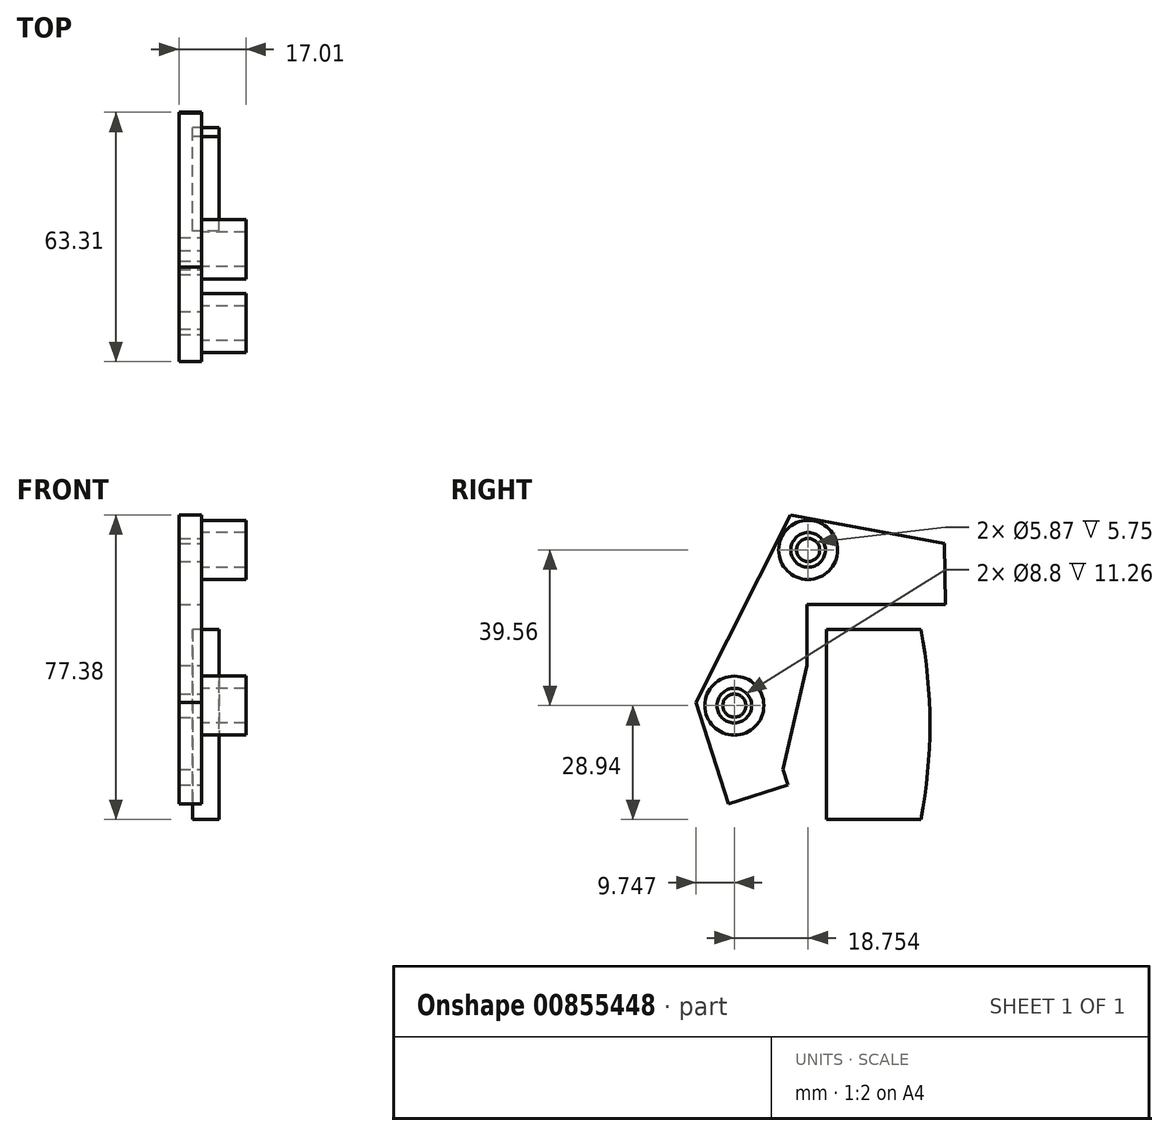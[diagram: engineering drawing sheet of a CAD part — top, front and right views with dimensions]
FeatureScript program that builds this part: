
annotation { "Feature Type Name" : "Feature", "Feature Type Description" : "" }
export const myFeature = defineFeature(function(context is Context, id is Id, definition is map)
    precondition{}
    {
        {
            var Q0;
            Q0=qCreatedBy(makeId("Right.planeOp"),FACE);
            var sketch = newSketch(context, id + "F0", { "sketchPlane" : qUnion([Q0])});
            skLineSegment(sketch, "E0.bottom", {"start": v(101.64, 24.15) * mm, "end": v(125.64, 24.15) * mm});
            skLineSegment(sketch, "E0.top", {"start": v(101.64, -24.15) * mm, "end": v(125.64, -24.15) * mm});
            skLineSegment(sketch, "E0.left", {"start": v(101.64, 24.15) * mm, "end": v(101.64, -24.15) * mm});
            skLineSegment(sketch, "E0.right", {"start": v(125.64, 24.15) * mm, "end": v(125.64, -24.15) * mm});
            skCircle(sketch, "E1", {"center": v(0, 0) * mm, "radius": 127.94 * mm});
            skPoint(sketch, "E1.third.point", {"position": v(127.94, 0) * mm});
            skPoint(sketch, "E1.third.point.positionSnap0", {"position": v(125.64, 0) * mm});
            skSolve(sketch);
        }
        {
            var Q0;
            Q0=makeQuery(id+"F0.imprint","IMPRINT",FACE,{"disambiguationData":[TD([[makeQuery(id+"F0.imprint","IMPRINT",EDGE,{"derivedFrom":sQuery(id+"F0.wireOp",EDGE,"E0.bottom")}),-1.0]])]});
            var Q1;
            {var subQ0=sQuery(id+"F0.wireOp",EDGE,"E0.right");Q1=makeQuery(id+"F0.imprint","IMPRINT",FACE,{"disambiguationData":[TD([[makeQuery(id+"F0.imprint","IMPRINT",EDGE,{"derivedFrom":subQ0}),1.0]])]});}
            extrude(context, id + "F1", {"entities" : qUnion([Q0, Q1]), "depth" : 6.8 * mm, "offsetDistance" : 25 * mm});
        }
        {
            var Q0;
            Q0=makeQuery(id+"F1.opExtrude","CAP_FACE",FACE,{"disambiguationData":[OSD([sQuery(id+"F0.wireOp",EDGE,"E0.bottom"),sQuery(id+"F0.wireOp",EDGE,"E0.top"),sQuery(id+"F0.wireOp",EDGE,"E0.left"),sQuery(id+"F0.wireOp",EDGE,"E1")])],"isStart":true});
            cPlane(context, id + "F2", {"entities" : qUnion([Q0]), "cplaneType" : CPlaneType.OFFSET, "offset" : 2.3 * mm, "oppositeDirection" : true, "width" : 150 * mm, "height" : 150 * mm});
        }
        {
            var Q0;
            Q0=qCreatedBy(id+"F2.planeOp",FACE);
            var sketch = newSketch(context, id + "F3", { "sketchPlane" : qUnion([Q0])});
            skLineSegment(sketch, "E2.0.0", {"start": v(-101.64, 24.15) * mm, "end": v(-101.64, -24.15) * mm});
            skLineSegment(sketch, "E2.0.1", {"start": v(-101.64, -24.15) * mm, "end": v(-125.64, -24.15) * mm});
            skArc(sketch, "E2.0.2", {"start": v(-125.64, -24.15) * mm, "mid": v(-127.94, 0) * mm, "end": v(-125.64, 24.15) * mm});
            skLineSegment(sketch, "E2.0.3", {"start": v(-125.64, 24.15) * mm, "end": v(-101.64, 24.15) * mm});
            skPoint(sketch, "E3", {"position": v(-78.26, 4.8) * mm});
            skPoint(sketch, "E4", {"position": v(-97.01, 44.35) * mm});
            skLineSegment(sketch, "E5", {"start": v(-131.61, 45.95) * mm, "end": v(-92.51, 53.23) * mm});
            skLineSegment(sketch, "E6", {"start": v(-92.51, 53.23) * mm, "end": v(-68.51, 5.54) * mm});
            skLineSegment(sketch, "E7", {"start": v(-68.51, 5.54) * mm, "end": v(-76.8, -20.15) * mm});
            skLineSegment(sketch, "E8", {"start": v(-76.8, -20.15) * mm, "end": v(-91.83, -15.3) * mm});
            skLineSegment(sketch, "E9", {"start": v(-91.83, -15.3) * mm, "end": v(-90.57, -11.4) * mm});
            skLineSegment(sketch, "E10", {"start": v(-90.57, -11.4) * mm, "end": v(-96.68, 15.04) * mm});
            skLineSegment(sketch, "E11", {"start": v(-96.68, 15.04) * mm, "end": v(-96.68, 30.5) * mm});
            skLineSegment(sketch, "E12", {"start": v(-96.68, 30.5) * mm, "end": v(-131.82, 30.5) * mm});
            skLineSegment(sketch, "E13", {"start": v(-131.82, 30.5) * mm, "end": v(-131.61, 45.95) * mm});
            skCircle(sketch, "E14", {"center": v(-97.01, 44.35) * mm, "radius": 2.94 * mm});
            skCircle(sketch, "E15", {"center": v(-78.26, 4.8) * mm, "radius": 2.94 * mm});
            skSolve(sketch);
        }
        {
            var Q0;
            Q0=makeQuery(id+"F3.imprint","IMPRINT",FACE,{"disambiguationData":[TD([[makeQuery(id+"F3.imprint","IMPRINT",EDGE,{"derivedFrom":sQuery(id+"F3.wireOp",EDGE,"E5")}),-1.0]])]});
            extrude(context, id + "F4", {"entities" : qUnion([Q0]), "depth" : 5.75 * mm, "offsetDistance" : 25 * mm});
        }
        {
            var Q0;
            Q0=makeQuery(id+"F4.opExtrude","CAP_FACE",FACE,{"disambiguationData":[OSD([sQuery(id+"F3.wireOp",EDGE,"E5"),sQuery(id+"F3.wireOp",EDGE,"E6"),sQuery(id+"F3.wireOp",EDGE,"E7"),sQuery(id+"F3.wireOp",EDGE,"E8"),sQuery(id+"F3.wireOp",EDGE,"E9"),sQuery(id+"F3.wireOp",EDGE,"E10"),sQuery(id+"F3.wireOp",EDGE,"E11"),sQuery(id+"F3.wireOp",EDGE,"E12"),sQuery(id+"F3.wireOp",EDGE,"E13"),sQuery(id+"F3.wireOp",EDGE,"E14"),sQuery(id+"F3.wireOp",EDGE,"E15")])],"isStart":true});
            var sketch = newSketch(context, id + "F5", { "sketchPlane" : qUnion([Q0])});
            skCircle(sketch, "E16", {"center": v(97.01, 44.35) * mm, "radius": 7.5 * mm});
            skCircle(sketch, "E17", {"center": v(97.01, 44.35) * mm, "radius": 4.4 * mm});
            skCircle(sketch, "E18", {"center": v(78.26, 4.8) * mm, "radius": 7.5 * mm});
            skCircle(sketch, "E19", {"center": v(78.26, 4.8) * mm, "radius": 4.4 * mm});
            skSolve(sketch);
        }
        {
            var Q0;
            Q0=makeQuery(id+"F5.imprint","IMPRINT",FACE,{"disambiguationData":[TD([[makeQuery(id+"F5.imprint","IMPRINT",EDGE,{"derivedFrom":sQuery(id+"F5.wireOp",EDGE,"E16")}),1.0]])]});
            var Q1;
            Q1=makeQuery(id+"F5.imprint","IMPRINT",FACE,{"disambiguationData":[TD([[makeQuery(id+"F5.imprint","IMPRINT",EDGE,{"derivedFrom":sQuery(id+"F5.wireOp",EDGE,"E18")}),1.0]])]});
            extrude(context, id + "F6", {"entities" : qUnion([Q0, Q1]), "operationType" : NewBodyOperationType.ADD, "depth" : 11.26 * mm, "offsetDistance" : 25 * mm});
        }
    });
